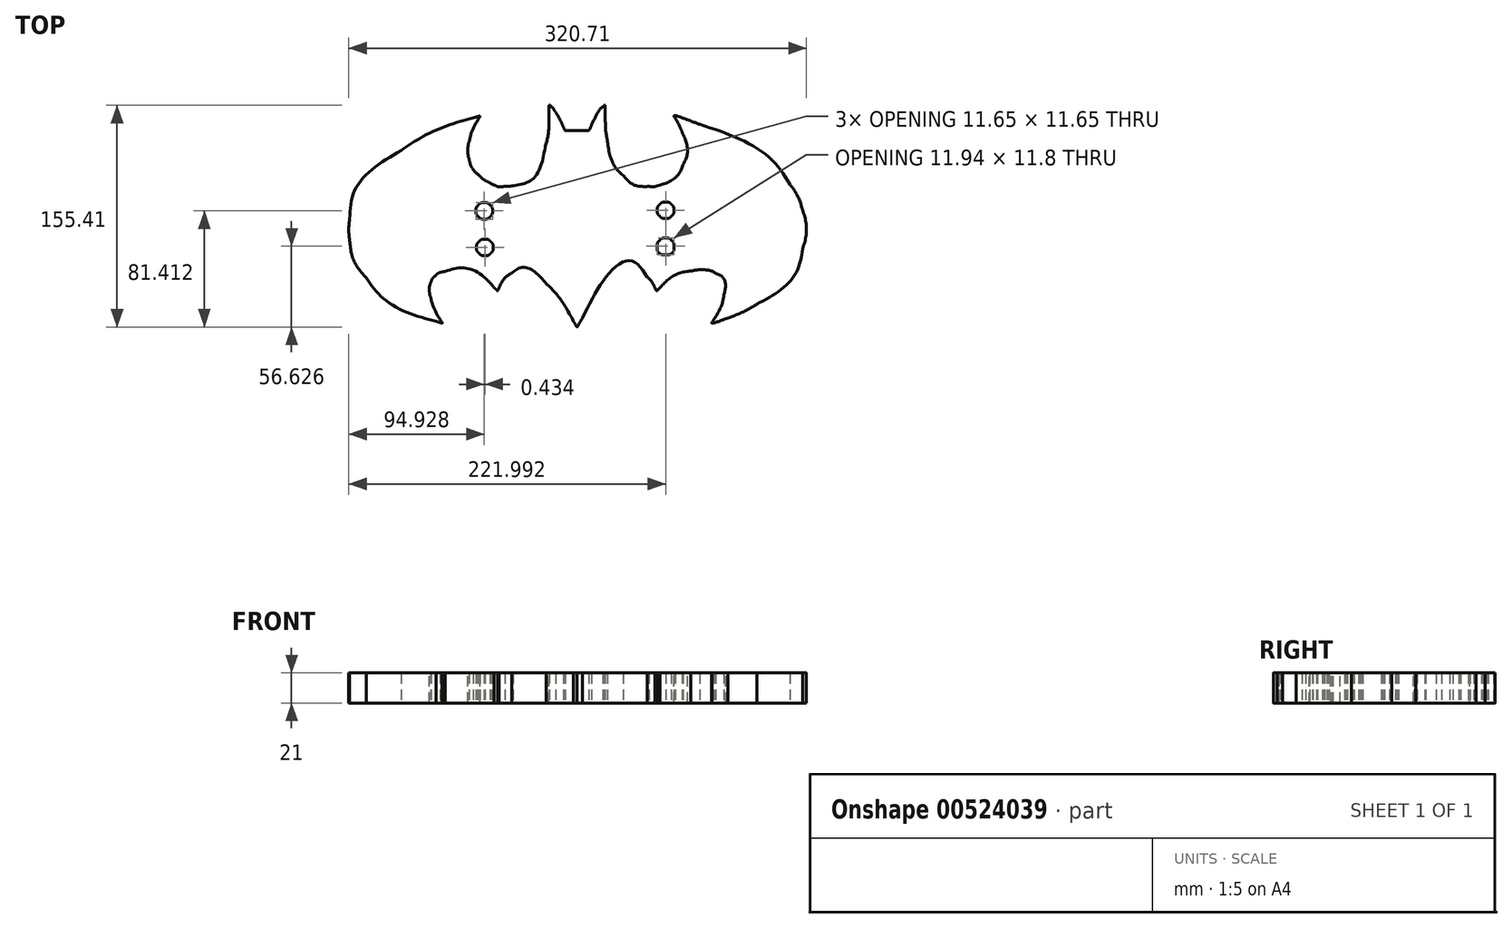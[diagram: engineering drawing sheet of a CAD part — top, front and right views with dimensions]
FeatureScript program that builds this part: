
annotation { "Feature Type Name" : "Feature", "Feature Type Description" : "" }
export const myFeature = defineFeature(function(context is Context, id is Id, definition is map)
    precondition{}
    {
        {
            var Q0;
            Q0=qCreatedBy(makeId("Top.planeOp"),FACE);
            var sketch = newSketch(context, id + "F0", { "sketchPlane" : qUnion([Q0])});
            skFitSpline(sketch, "E0", {"points": [v(-25.42, -109.49) * mm, v(-31.78, -98.34) * mm, v(-38.34, -89.27) * mm, v(-44.38, -83.26) * mm]});
            skFitSpline(sketch, "E1", {"points": [v(-44.38, -83.26) * mm, v(-53.38, -74.31) * mm, v(-61.67, -71.79) * mm, v(-68.7, -75.85) * mm]});
            skFitSpline(sketch, "E2", {"points": [v(-68.7, -75.85) * mm, v(-71.86, -77.67) * mm, v(-75.35, -81.72) * mm, v(-77.54, -86.1) * mm]});
            skFitSpline(sketch, "E3", {"points": [v(-77.54, -86.1) * mm, v(-78.1, -87.2) * mm, v(-78.58, -88.15) * mm, v(-78.62, -88.2) * mm]});
            skFitSpline(sketch, "E4", {"points": [v(-78.62, -88.2) * mm, v(-78.65, -88.23) * mm, v(-79.7, -87.28) * mm, v(-80.94, -86.07) * mm]});
            skFitSpline(sketch, "E5", {"points": [v(-80.94, -86.07) * mm, v(-90.98, -76.3) * mm, v(-103.44, -72.15) * mm, v(-115.43, -74.6) * mm]});
            skFitSpline(sketch, "E6", {"points": [v(-115.43, -74.6) * mm, v(-119.02, -75.33) * mm, v(-120.37, -75.94) * mm, v(-122.25, -77.7) * mm]});
            skFitSpline(sketch, "E7", {"points": [v(-122.25, -77.7) * mm, v(-123.9, -79.24) * mm, v(-124.67, -80.42) * mm, v(-125.45, -82.63) * mm]});
            skFitSpline(sketch, "E8", {"points": [v(-125.45, -82.63) * mm, v(-126.32, -85.13) * mm, v(-126.26, -89.8) * mm, v(-125.32, -93.43) * mm]});
            skFitSpline(sketch, "E9", {"points": [v(-125.32, -93.43) * mm, v(-124.14, -97.95) * mm, v(-121.7, -103.46) * mm, v(-118.69, -108.45) * mm]});
            skFitSpline(sketch, "E10", {"points": [v(-118.69, -108.45) * mm, v(-117.93, -109.7) * mm, v(-117.36, -110.77) * mm, v(-117.41, -110.82) * mm]});
            skFitSpline(sketch, "E11", {"points": [v(-117.41, -110.82) * mm, v(-117.47, -110.88) * mm, v(-119.32, -110.36) * mm, v(-121.53, -109.68) * mm]});
            skFitSpline(sketch, "E12", {"points": [v(-121.53, -109.68) * mm, v(-142.47, -103.18) * mm, v(-160.37, -92.06) * mm, v(-170.6, -79.2) * mm]});
            skFitSpline(sketch, "E13", {"points": [v(-170.6, -79.2) * mm, v(-177.1, -71.04) * mm, v(-180.83, -62.56) * mm, v(-182.17, -52.92) * mm]});
            skFitSpline(sketch, "E14", {"points": [v(-182.17, -52.92) * mm, v(-182.74, -48.85) * mm, v(-182.74, -41.81) * mm, v(-182.18, -37.96) * mm]});
            skFitSpline(sketch, "E15", {"points": [v(-182.18, -37.96) * mm, v(-179.57, -20.06) * mm, v(-167.51, -3.98) * mm, v(-146.19, 10.03) * mm]});
            skFitSpline(sketch, "E16", {"points": [v(-146.19, 10.03) * mm, v(-132.55, 19) * mm, v(-113.86, 27.5) * mm, v(-95.74, 32.96) * mm]});
            skFitSpline(sketch, "E17", {"points": [v(-95.74, 32.96) * mm, v(-93.15, 33.74) * mm, v(-90.98, 34.35) * mm, v(-90.93, 34.3) * mm]});
            skFitSpline(sketch, "E18", {"points": [v(-90.93, 34.3) * mm, v(-90.89, 34.27) * mm, v(-91.4, 33.27) * mm, v(-92.07, 32.1) * mm]});
            skFitSpline(sketch, "E19", {"points": [v(-92.07, 32.1) * mm, v(-95.08, 26.89) * mm, v(-97.22, 21.69) * mm, v(-98.48, 16.52) * mm]});
            skFitSpline(sketch, "E20", {"points": [v(-98.48, 16.52) * mm, v(-99.25, 13.37) * mm, v(-99.32, 7.25) * mm, v(-98.63, 4.44) * mm]});
            skFitSpline(sketch, "E21", {"points": [v(-98.63, 4.44) * mm, v(-97.53, 0) * mm, v(-95.38, -3.64) * mm, v(-91.9, -6.98) * mm]});
            skFitSpline(sketch, "E22", {"points": [v(-91.9, -6.98) * mm, v(-89.21, -9.56) * mm, v(-87.26, -10.92) * mm, v(-83.7, -12.7) * mm]});
            skFitSpline(sketch, "E23", {"points": [v(-83.7, -12.7) * mm, v(-79.1, -15) * mm, v(-77.97, -15.26) * mm, v(-73.39, -15.09) * mm]});
            skFitSpline(sketch, "E24", {"points": [v(-73.39, -15.09) * mm, v(-71.22, -15) * mm, v(-68.69, -14.75) * mm, v(-67.76, -14.51) * mm]});
            skFitSpline(sketch, "E25", {"points": [v(-67.76, -14.51) * mm, v(-56.6, -11.73) * mm, v(-49.15, -2.87) * mm, v(-45.3, 12.2) * mm]});
            skFitSpline(sketch, "E26", {"points": [v(-45.3, 12.2) * mm, v(-43.44, 19.53) * mm, v(-42.62, 26.76) * mm, v(-42.62, 36) * mm]});
            skFitSpline(sketch, "E27", {"points": [v(-42.62, 36) * mm, v(-42.62, 40.26) * mm, v(-42.53, 41.73) * mm, v(-42.3, 41.73) * mm]});
            skFitSpline(sketch, "E28", {"points": [v(-42.3, 41.73) * mm, v(-41.78, 41.73) * mm, v(-39.34, 39.06) * mm, v(-38, 37.02) * mm]});
            skFitSpline(sketch, "E29", {"points": [v(-38, 37.02) * mm, v(-36.45, 34.66) * mm, v(-34.11, 30.26) * mm, v(-32.62, 26.9) * mm]});
            skFitSpline(sketch, "E30", {"points": [v(-32.62, 26.9) * mm, v(-32, 25.5) * mm, v(-31.34, 24.25) * mm, v(-31.18, 24.14) * mm]});
            skFitSpline(sketch, "E31", {"points": [v(-31.18, 24.14) * mm, v(-31.02, 24.03) * mm, v(-27.3, 23.94) * mm, v(-22.93, 23.94) * mm]});
            skFitSpline(sketch, "E32", {"points": [v(-22.93, 23.94) * mm, v(-18.55, 23.94) * mm, v(-14.84, 24.03) * mm, v(-14.67, 24.14) * mm]});
            skFitSpline(sketch, "E33", {"points": [v(-14.67, 24.14) * mm, v(-14.5, 24.25) * mm, v(-13.73, 25.74) * mm, v(-12.94, 27.44) * mm]});
            skFitSpline(sketch, "E34", {"points": [v(-12.94, 27.44) * mm, v(-10, 33.8) * mm, v(-6.89, 38.93) * mm, v(-4.83, 40.79) * mm]});
            skFitSpline(sketch, "E35", {"points": [v(-4.83, 40.79) * mm, v(-4.25, 41.3) * mm, v(-3.68, 41.73) * mm, v(-3.55, 41.73) * mm]});
            skFitSpline(sketch, "E36", {"points": [v(-3.55, 41.73) * mm, v(-3.42, 41.73) * mm, v(-3.24, 38.3) * mm, v(-3.16, 34.12) * mm]});
            skFitSpline(sketch, "E37", {"points": [v(-3.16, 34.12) * mm, v(-3, 26.74) * mm, v(-2.7, 23.1) * mm, v(-1.77, 17.73) * mm]});
            skFitSpline(sketch, "E38", {"points": [v(-1.77, 17.73) * mm, v(0.08, 7.07) * mm, v(4.13, -2) * mm, v(9.43, -7.37) * mm]});
            skFitSpline(sketch, "E39", {"points": [v(9.43, -7.37) * mm, v(14.56, -12.56) * mm, v(19.84, -14.81) * mm, v(27.53, -15.1) * mm]});
            skFitSpline(sketch, "E40", {"points": [v(27.53, -15.1) * mm, v(31.13, -15.23) * mm, v(31.62, -15.19) * mm, v(33.33, -14.62) * mm]});
            skFitSpline(sketch, "E41", {"points": [v(33.33, -14.62) * mm, v(41.5, -11.92) * mm, v(48.54, -6.08) * mm, v(51.37, 0.33) * mm]});
            skFitSpline(sketch, "E42", {"points": [v(51.37, 0.33) * mm, v(54.2, 6.71) * mm, v(53.96, 14.57) * mm, v(50.69, 23) * mm]});
            skFitSpline(sketch, "E43", {"points": [v(50.69, 23) * mm, v(49.73, 25.44) * mm, v(47.32, 30.34) * mm, v(45.95, 32.6) * mm]});
            skFitSpline(sketch, "E44", {"points": [v(45.95, 32.6) * mm, v(45.44, 33.44) * mm, v(45.03, 34.18) * mm, v(45.03, 34.26) * mm]});
            skFitSpline(sketch, "E45", {"points": [v(45.03, 34.26) * mm, v(45.03, 34.63) * mm, v(56.06, 31.1) * mm, v(63.1, 28.46) * mm]});
            skFitSpline(sketch, "E46", {"points": [v(63.1, 28.46) * mm, v(92.29, 17.55) * mm, v(114.45, 2.76) * mm, v(126.26, -13.68) * mm]});
            skFitSpline(sketch, "E47", {"points": [v(126.26, -13.68) * mm, v(129.93, -18.8) * mm, v(133.22, -25.33) * mm, v(134.71, -30.48) * mm]});
            skFitSpline(sketch, "E48", {"points": [v(134.71, -30.48) * mm, v(137.38, -39.68) * mm, v(137.55, -49.44) * mm, v(135.2, -58.72) * mm]});
            skFitSpline(sketch, "E49", {"points": [v(135.2, -58.72) * mm, v(131.4, -73.8) * mm, v(120.39, -87.13) * mm, v(103.18, -97.49) * mm]});
            skFitSpline(sketch, "E50", {"points": [v(103.18, -97.49) * mm, v(97, -101.2) * mm, v(89.88, -104.61) * mm, v(82.68, -107.3) * mm]});
            skFitSpline(sketch, "E51", {"points": [v(82.68, -107.3) * mm, v(79, -108.67) * mm, v(71.7, -110.97) * mm, v(71.55, -110.81) * mm]});
            skFitSpline(sketch, "E52", {"points": [v(71.55, -110.81) * mm, v(71.5, -110.75) * mm, v(72.07, -109.69) * mm, v(72.84, -108.45) * mm]});
            skFitSpline(sketch, "E53", {"points": [v(72.84, -108.45) * mm, v(76.28, -102.9) * mm, v(79.1, -95.99) * mm, v(79.98, -90.9) * mm]});
            skFitSpline(sketch, "E54", {"points": [v(79.98, -90.9) * mm, v(81.16, -84.12) * mm, v(79, -78.65) * mm, v(74.1, -75.98) * mm]});
            skFitSpline(sketch, "E55", {"points": [v(74.1, -75.98) * mm, v(70.82, -74.2) * mm, v(62.57, -73.43) * mm, v(56.88, -74.38) * mm]});
            skFitSpline(sketch, "E56", {"points": [v(56.88, -74.38) * mm, v(49.24, -75.67) * mm, v(41.57, -79.78) * mm, v(35.26, -85.98) * mm]});
            skFitSpline(sketch, "E57", {"points": [v(35.26, -85.98) * mm, v(33.95, -87.27) * mm, v(32.83, -88.27) * mm, v(32.78, -88.22) * mm]});
            skFitSpline(sketch, "E58", {"points": [v(32.78, -88.22) * mm, v(32.73, -88.16) * mm, v(32.23, -87.2) * mm, v(31.68, -86.1) * mm]});
            skFitSpline(sketch, "E59", {"points": [v(31.68, -86.1) * mm, v(30.27, -83.28) * mm, v(28.36, -80.6) * mm, v(26.37, -78.63) * mm]});
            skFitSpline(sketch, "E60", {"points": [v(26.37, -78.63) * mm, v(14.6, -67.04) * mm, v(-1.45, -77.17) * mm, v(-19.2, -107.4) * mm]});
            skFitSpline(sketch, "E61", {"points": [v(-19.2, -107.4) * mm, v(-20.46, -109.55) * mm, v(-21.78, -111.82) * mm, v(-22.13, -112.45) * mm]});
            skFitSpline(sketch, "E62", {"points": [v(-22.13, -112.45) * mm, v(-22.47, -113.09) * mm, v(-22.83, -113.6) * mm, v(-22.91, -113.6) * mm]});
            skFitSpline(sketch, "E63", {"points": [v(-22.91, -113.6) * mm, v(-23, -113.6) * mm, v(-24.13, -111.75) * mm, v(-25.42, -109.49) * mm]});
            skFitSpline(sketch, "E64", {"points": [v(-82.15, -32.2) * mm, v(-82.15, -33.73) * mm, v(-82.76, -35.2) * mm, v(-83.84, -36.29) * mm]});
            skFitSpline(sketch, "E65", {"points": [v(-83.84, -36.29) * mm, v(-84.93, -37.37) * mm, v(-86.4, -37.98) * mm, v(-87.93, -37.98) * mm]});
            skFitSpline(sketch, "E66", {"points": [v(-87.93, -37.98) * mm, v(-89.47, -37.98) * mm, v(-90.94, -37.37) * mm, v(-92.02, -36.29) * mm]});
            skFitSpline(sketch, "E67", {"points": [v(-92.02, -36.29) * mm, v(-93.1, -35.2) * mm, v(-93.72, -33.73) * mm, v(-93.72, -32.2) * mm]});
            skFitSpline(sketch, "E68", {"points": [v(-93.72, -32.2) * mm, v(-93.72, -30.66) * mm, v(-93.1, -29.2) * mm, v(-92.02, -28.1) * mm]});
            skFitSpline(sketch, "E69", {"points": [v(-92.02, -28.1) * mm, v(-90.94, -27.02) * mm, v(-89.47, -26.41) * mm, v(-87.93, -26.41) * mm]});
            skFitSpline(sketch, "E70", {"points": [v(-87.93, -26.41) * mm, v(-86.4, -26.41) * mm, v(-84.93, -27.02) * mm, v(-83.84, -28.1) * mm]});
            skFitSpline(sketch, "E71", {"points": [v(-83.84, -28.1) * mm, v(-82.76, -29.2) * mm, v(-82.15, -30.66) * mm, v(-82.15, -32.2) * mm]});
            skFitSpline(sketch, "E72", {"points": [v(-81.71, -57.8) * mm, v(-81.71, -59.34) * mm, v(-82.32, -60.81) * mm, v(-83.4, -61.9) * mm]});
            skFitSpline(sketch, "E73", {"points": [v(-83.4, -61.9) * mm, v(-84.5, -62.98) * mm, v(-85.96, -63.6) * mm, v(-87.5, -63.6) * mm]});
            skFitSpline(sketch, "E74", {"points": [v(-87.5, -63.6) * mm, v(-89.03, -63.6) * mm, v(-90.5, -62.98) * mm, v(-91.59, -61.9) * mm]});
            skFitSpline(sketch, "E75", {"points": [v(-91.59, -61.9) * mm, v(-92.67, -60.81) * mm, v(-93.28, -59.34) * mm, v(-93.28, -57.8) * mm]});
            skFitSpline(sketch, "E76", {"points": [v(-93.28, -57.8) * mm, v(-93.28, -56.27) * mm, v(-92.67, -54.8) * mm, v(-91.59, -53.72) * mm]});
            skFitSpline(sketch, "E77", {"points": [v(-91.59, -53.72) * mm, v(-90.5, -52.63) * mm, v(-89.03, -52.02) * mm, v(-87.5, -52.02) * mm]});
            skFitSpline(sketch, "E78", {"points": [v(-87.5, -52.02) * mm, v(-85.96, -52.02) * mm, v(-84.5, -52.63) * mm, v(-83.4, -53.72) * mm]});
            skFitSpline(sketch, "E79", {"points": [v(-83.4, -53.72) * mm, v(-82.32, -54.8) * mm, v(-81.71, -56.27) * mm, v(-81.71, -57.8) * mm]});
            skFitSpline(sketch, "E80", {"points": [v(44.92, -31.76) * mm, v(44.92, -33.3) * mm, v(44.3, -34.77) * mm, v(43.22, -35.85) * mm]});
            skFitSpline(sketch, "E81", {"points": [v(43.22, -35.85) * mm, v(42.14, -36.94) * mm, v(40.67, -37.55) * mm, v(39.13, -37.55) * mm]});
            skFitSpline(sketch, "E82", {"points": [v(39.13, -37.55) * mm, v(37.6, -37.55) * mm, v(36.13, -36.94) * mm, v(35.04, -35.85) * mm]});
            skFitSpline(sketch, "E83", {"points": [v(35.04, -35.85) * mm, v(33.96, -34.77) * mm, v(33.35, -33.3) * mm, v(33.35, -31.76) * mm]});
            skFitSpline(sketch, "E84", {"points": [v(33.35, -31.76) * mm, v(33.35, -30.23) * mm, v(33.96, -28.76) * mm, v(35.04, -27.67) * mm]});
            skFitSpline(sketch, "E85", {"points": [v(35.04, -27.67) * mm, v(36.13, -26.59) * mm, v(37.6, -25.98) * mm, v(39.13, -25.98) * mm]});
            skFitSpline(sketch, "E86", {"points": [v(39.13, -25.98) * mm, v(40.67, -25.98) * mm, v(42.14, -26.59) * mm, v(43.22, -27.67) * mm]});
            skFitSpline(sketch, "E87", {"points": [v(43.22, -27.67) * mm, v(44.3, -28.76) * mm, v(44.92, -30.23) * mm, v(44.92, -31.76) * mm]});
            skFitSpline(sketch, "E88", {"points": [v(44.92, -56.91) * mm, v(44.92, -60.1) * mm, v(42.33, -62.7) * mm, v(39.13, -62.7) * mm]});
            skFitSpline(sketch, "E89", {"points": [v(39.13, -62.7) * mm, v(35.94, -62.7) * mm, v(33.35, -60.1) * mm, v(33.35, -56.91) * mm]});
            skFitSpline(sketch, "E90", {"points": [v(33.35, -56.91) * mm, v(33.35, -55.38) * mm, v(33.96, -53.9) * mm, v(35.04, -52.82) * mm]});
            skFitSpline(sketch, "E91", {"points": [v(35.04, -52.82) * mm, v(36.13, -51.74) * mm, v(37.6, -51.13) * mm, v(39.13, -51.13) * mm]});
            skFitSpline(sketch, "E92", {"points": [v(39.13, -51.13) * mm, v(40.67, -51.13) * mm, v(42.14, -51.74) * mm, v(43.22, -52.82) * mm]});
            skFitSpline(sketch, "E93", {"points": [v(43.22, -52.82) * mm, v(44.3, -53.9) * mm, v(44.92, -55.38) * mm, v(44.92, -56.91) * mm]});
            skSolve(sketch);
        }
        {
            var Q0;
            Q0 = qSketchRegion(id + "F0", true);
            extrude(context, id + "F1", {"entities" : qUnion([Q0]), "depth" : 21 * mm, "offsetDistance" : 25 * mm});
        }
    });
